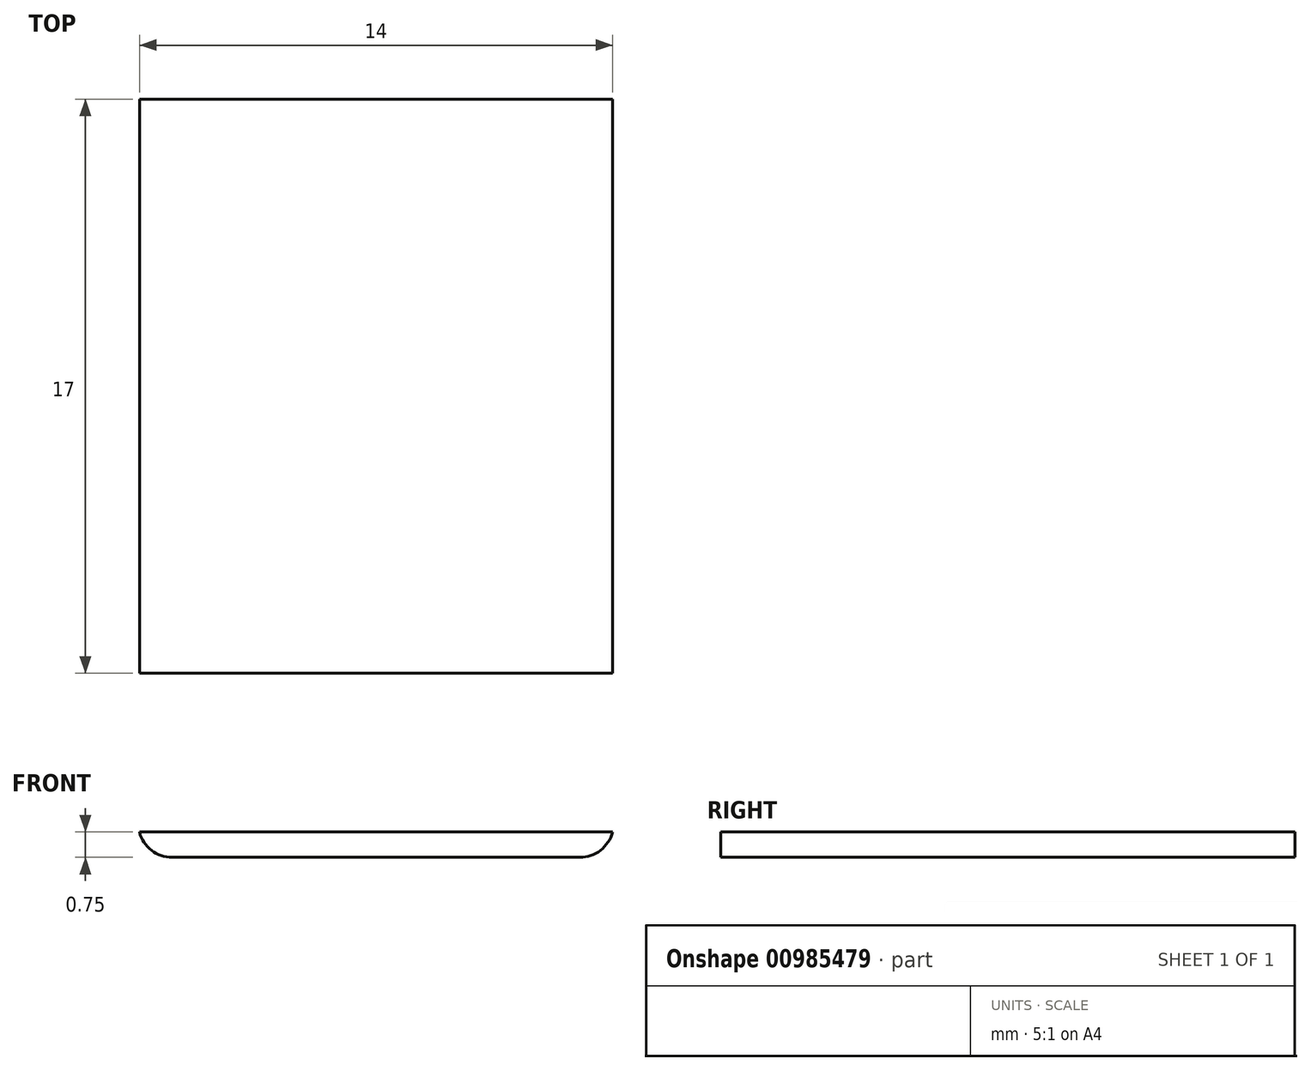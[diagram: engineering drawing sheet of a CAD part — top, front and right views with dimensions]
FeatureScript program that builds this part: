
annotation { "Feature Type Name" : "Feature", "Feature Type Description" : "" }
export const myFeature = defineFeature(function(context is Context, id is Id, definition is map)
    precondition{}
    {
        {
            var Q0;
            Q0=qCreatedBy(makeId("Top.planeOp"),FACE);
            var sketch = newSketch(context, id + "F0", { "sketchPlane" : qUnion([Q0])});
            skLineSegment(sketch, "E0.bottom", {"start": v(0, 0) * mm, "end": v(14, 0) * mm});
            skLineSegment(sketch, "E0.top", {"start": v(0, 17) * mm, "end": v(14, 17) * mm});
            skLineSegment(sketch, "E0.left", {"start": v(0, 0) * mm, "end": v(0, 17) * mm});
            skLineSegment(sketch, "E0.right", {"start": v(14, 0) * mm, "end": v(14, 17) * mm});
            skSolve(sketch);
        }
        {
            var Q0;
            Q0=qSketchRegion(id+"F0",true);
            extrude(context, id + "F1", {"entities" : qUnion([Q0]), "depth" : .75 * mm});
        }
        {
            var Q0;
            Q0=makeQuery(id+"F1.opExtrude","CAP_EDGE",EDGE,{"disambiguationData":[OSD([sQuery(id+"F0.wireOp",EDGE,"E0.right")])],"isStart":true});
            var Q1;
            Q1=makeQuery(id+"F1.opExtrude","CAP_EDGE",EDGE,{"disambiguationData":[OSD([sQuery(id+"F0.wireOp",EDGE,"E0.left")])],"isStart":true});
            fillet(context, id + "F2", {"entities" : qUnion([Q0, Q1]), "radius" : 1 * mm, "tangentPropagation" : true, "allowEdgeOverflow" : false});
        }
    });
